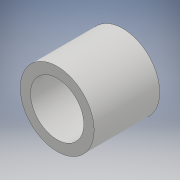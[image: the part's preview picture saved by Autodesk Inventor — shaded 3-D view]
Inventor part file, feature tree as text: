
AUTODESK INVENTOR PART (.ipt)
format: ipt  version: 2018 (Build 220112000, 112)  size: 224,256 bytes
history: native  units: mm
features: extrude x2, sketch x2
ambient origin geometry x8: Origin, YZ Plane, XZ Plane, XY Plane, X Axis, Y Axis, Z Axis, Center Point
bodies: Solid1 (feature_tree)
feature tree (4):
  extrude  "Extrusion1"  Depth=4.0mm
  extrude  "Extrusion2"  Depth=4.0mm
  sketch  "Sketch1"  dims[d0=4.0mm d1=3.25mm]
  sketch  "Sketch2"  dims[d2=4.0mm d3=0.0mm d4=4.5mm d5=4.0mm d6=0.0mm]
